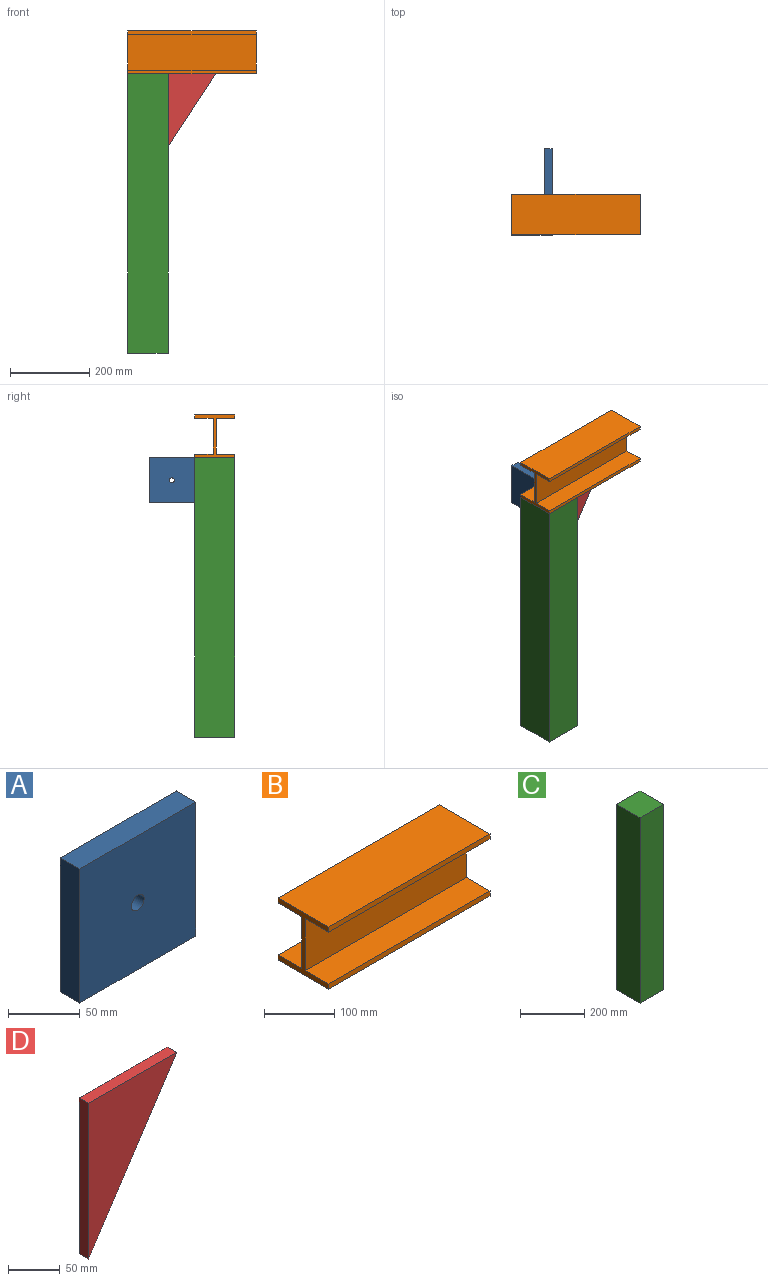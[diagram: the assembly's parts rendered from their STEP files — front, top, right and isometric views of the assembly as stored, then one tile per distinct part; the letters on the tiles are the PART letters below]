
ASSEMBLY  parts=4 mates=2
PART A: 7 faces, bbox 114.3x19.1x114.3 mm
  f0: plane 114.3x19.05mm, normal (0,0,1), area 2177.4mm2, adj f1,f3,f4,f5
  f1: plane 114.3x19.05mm, normal (-1,0,0), area 2177.4mm2, adj f0,f2,f4,f5
  f2: plane 114.3x19.05mm, normal (0,0,-1), area 2177.4mm2, adj f1,f3,f4,f5
  f3: plane 114.3x19.05mm, normal (1,0,0), area 2177.4mm2, adj f0,f2,f4,f5
  f4: plane 114.3x114.3mm, normal (0,-1,0), area 12937.8mm2, adj f0,f1,f2,f3,f6
  f5: plane 114.3x114.3mm, normal (0,1,0), area 12937.8mm2, adj f0,f1,f2,f3,f6
  f6: cylinder r=6.35mm len=19.05mm, axis (0,-1,0), area 760.1mm2, adj f4,f5
PART B: 14 faces, bbox 323.9x101.6x108 mm
  f0: plane 323.85x8.89mm, normal (0,-1,0), area 2879mm2, adj f1,f11,f12,f13
  f1: plane 323.85x101.6mm, normal (0,0,-1), area 32903.2mm2, adj f0,f2,f12,f13
  f2: plane 323.85x8.89mm, normal (0,1,0), area 2879mm2, adj f1,f3,f12,f13
  f3: plane 323.85x47.19mm, normal (0,0,1), area 15283.5mm2, adj f2,f4,f12,f13
  f4: plane 323.85x90.17mm, normal (0,1,0), area 29201.6mm2, adj f3,f5,f12,f13
  f5: plane 323.85x47.19mm, normal (0,0,-1), area 15283.5mm2, adj f4,f6,f12,f13
  f6: plane 323.85x8.89mm, normal (0,1,0), area 2879mm2, adj f5,f7,f12,f13
  f7: plane 323.85x101.6mm, normal (0,0,1), area 32903.2mm2, adj f6,f8,f12,f13
  f8: plane 323.85x8.89mm, normal (0,-1,0), area 2879mm2, adj f7,f9,f12,f13
  f9: plane 323.85x47.18mm, normal (0,0,-1), area 15279.4mm2, adj f8,f10,f12,f13
  f10: plane 323.85x90.17mm, normal (0,-1,0), area 29201.6mm2, adj f9,f11,f12,f13
  f11: plane 323.85x47.18mm, normal (0,0,1), area 15279.4mm2, adj f0,f10,f12,f13
  f12: plane 107.95x101.6mm, normal (1,0,0), area 2458mm2, adj f0,f1,f2,f3,f4,f5,f6,f7
  f13: plane 107.95x101.6mm, normal (-1,0,0), area 2458mm2, adj f0,f1,f2,f3,f4,f5,f6,f7
PART C: 6 faces, bbox 101.6x101.6x704.9 mm
  f0: plane 704.85x101.6mm, normal (-1,0,0), area 71612.8mm2, adj f1,f3,f4,f5
  f1: plane 704.85x101.6mm, normal (0,-1,0), area 71612.8mm2, adj f0,f2,f4,f5
  f2: plane 704.85x101.6mm, normal (1,0,0), area 71612.8mm2, adj f1,f3,f4,f5
  f3: plane 704.85x101.6mm, normal (0,1,0), area 71612.8mm2, adj f0,f2,f4,f5
  f4: plane 101.6x101.6mm, normal (0,0,1), area 10322.6mm2, adj f0,f1,f2,f3
  f5: plane 101.6x101.6mm, normal (0,0,-1), area 10322.6mm2, adj f0,f1,f2,f3
PART D: 5 faces, bbox 120.7x12.7x184.2 mm
  f0: plane 184.15x12.7mm, normal (-1,0,0), area 2338.7mm2, adj f1,f2,f3,f4
  f1: plane 184.15x120.65mm, normal (0.84,0,-0.55), area 2796mm2, adj f0,f2,f3,f4
  f2: plane 120.65x12.7mm, normal (0,0,1), area 1532.3mm2, adj f0,f1,f3,f4
  f3: plane 184.15x120.65mm, normal (0,-1,0), area 11108.8mm2, adj f0,f1,f2
  f4: plane 184.15x120.65mm, normal (0,1,0), area 11108.8mm2, adj f0,f1,f2
PLACE A rot(axis=(0,0,-1),90deg) t=(-540.9,-233.06,219.38)mm
PLACE B t=(-642.5,-370.91,307.49)mm
PLACE C t=(-642.5,-370.91,-397.36)mm
PLACE D t=(-479.45,-313.76,180.32)mm
MATE slider A.f3 <-> C.f3  axis (0,-1,0) through (-540.9,-269.31,307.49)mm
MATE planar D.f0 <-> C.f2  axis (-1,0,0) through (-540.9,-320.11,215.42)mm
